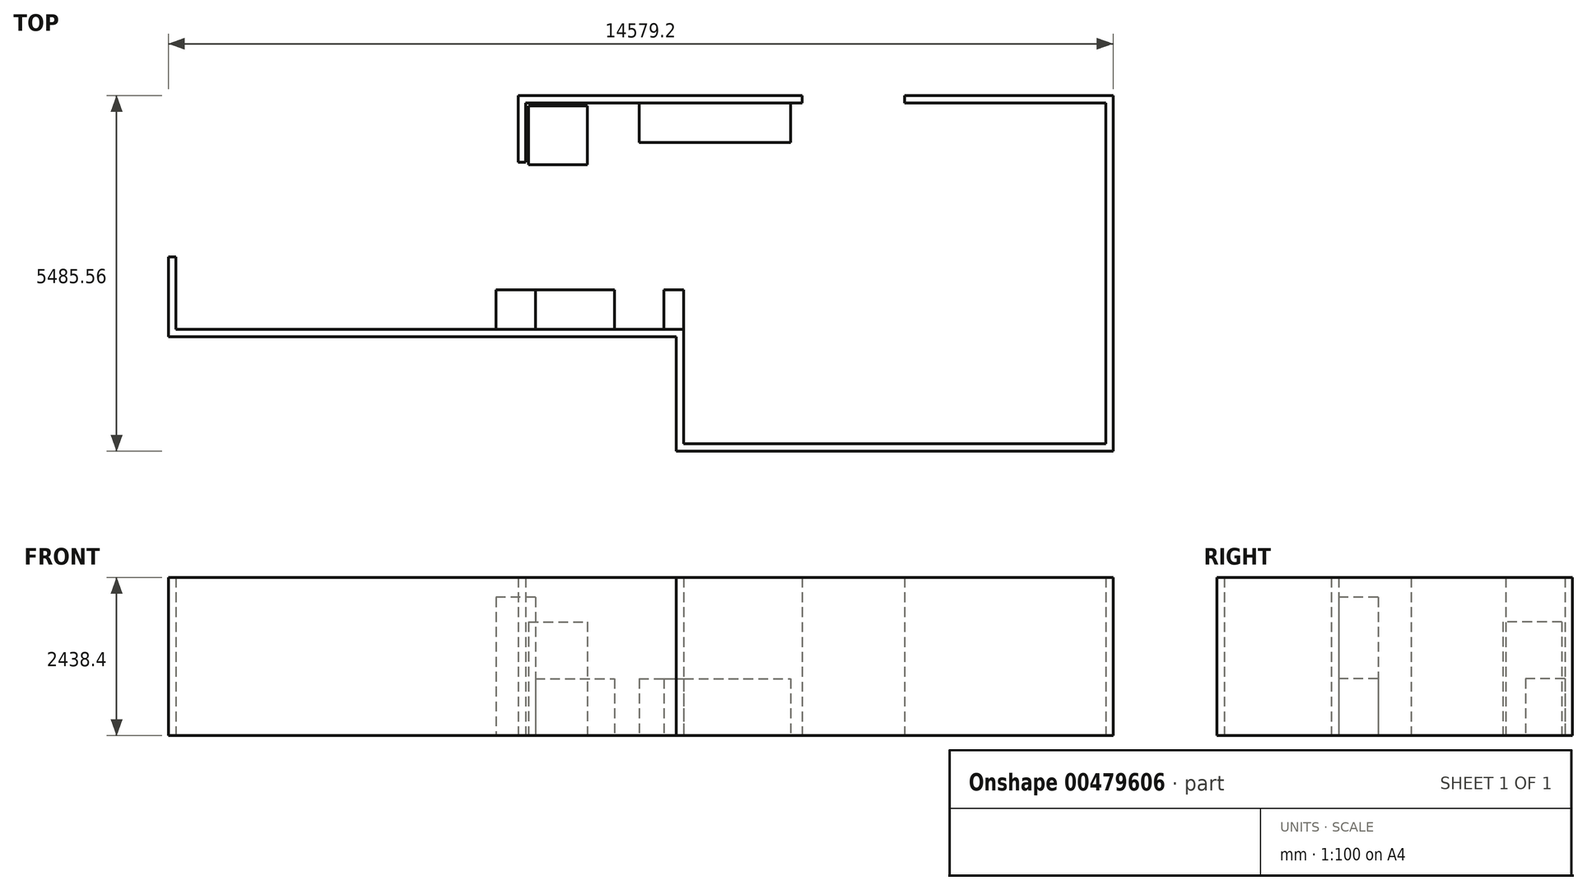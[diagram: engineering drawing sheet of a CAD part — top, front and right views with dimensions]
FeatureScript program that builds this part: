
annotation { "Feature Type Name" : "Feature", "Feature Type Description" : "" }
export const myFeature = defineFeature(function(context is Context, id is Id, definition is map)
    precondition{}
    {
        {
            var Q0;
            Q0=qCreatedBy(makeId("Top.planeOp"),FACE);
            var sketch = newSketch(context, id + "F0", { "sketchPlane" : qUnion([Q0])});
            skLineSegment(sketch, "E0.bottom", {"start": v(-1558.2, 1261.6) * mm, "end": v(-1443.9, 1261.6) * mm});
            skLineSegment(sketch, "E0.top", {"start": v(-1558.2, 232.9) * mm, "end": v(-1443.9, 232.9) * mm});
            skLineSegment(sketch, "E0.left", {"start": v(-1558.2, 1261.6) * mm, "end": v(-1558.2, 232.9) * mm});
            skLineSegment(sketch, "E0.right", {"start": v(-1443.9, 1147.3) * mm, "end": v(-1443.9, 232.9) * mm});
            skLineSegment(sketch, "E1.bottom", {"start": v(-1443.9, 1261.6) * mm, "end": v(2823.3, 1261.6) * mm});
            skLineSegment(sketch, "E1.top", {"start": v(-1443.9, 1147.3) * mm, "end": v(2823.3, 1147.3) * mm});
            skLineSegment(sketch, "E1.right", {"start": v(2823.3, 1261.6) * mm, "end": v(2823.3, 1147.3) * mm});
            skLineSegment(sketch, "E2.bottom", {"start": v(-1558.2, -2345.2) * mm, "end": v(994.5, -2345.2) * mm});
            skLineSegment(sketch, "E2.top", {"start": v(-1558.2, -2459.5) * mm, "end": v(994.5, -2459.5) * mm});
            skLineSegment(sketch, "E2.left", {"start": v(-1558.2, -2345.2) * mm, "end": v(-1558.2, -2459.5) * mm});
            skLineSegment(sketch, "E2.right", {"start": v(994.5, -2345.2) * mm, "end": v(994.5, -2459.5) * mm});
            skLineSegment(sketch, "E3.bottom", {"start": v(-1558.2, -2345.2) * mm, "end": v(-2167.8, -2345.2) * mm});
            skLineSegment(sketch, "E3.top", {"start": v(-1558.2, -2459.5) * mm, "end": v(-2167.8, -2459.5) * mm});
            skLineSegment(sketch, "E3.right", {"start": v(-2167.8, -2345.2) * mm, "end": v(-2167.8, -2459.5) * mm});
            skLineSegment(sketch, "E4.bottom", {"start": v(994.5, -2345.2) * mm, "end": v(880.2, -2345.2) * mm});
            skLineSegment(sketch, "E4.top", {"start": v(994.5, -4223.95) * mm, "end": v(880.2, -4223.95) * mm});
            skLineSegment(sketch, "E4.left", {"start": v(994.5, -2345.2) * mm, "end": v(994.5, -4223.95) * mm});
            skLineSegment(sketch, "E4.right", {"start": v(880.2, -2345.2) * mm, "end": v(880.2, -4223.95) * mm});
            skLineSegment(sketch, "E5.bottom", {"start": v(4408.84, 1261.6) * mm, "end": v(7625.02, 1261.6) * mm});
            skLineSegment(sketch, "E5.top", {"start": v(4408.84, 1147.3) * mm, "end": v(7625.02, 1147.3) * mm});
            skLineSegment(sketch, "E5.left", {"start": v(4408.84, 1261.6) * mm, "end": v(4408.84, 1147.3) * mm});
            skLineSegment(sketch, "E5.right", {"start": v(7625.02, 1261.6) * mm, "end": v(7625.02, 1147.3) * mm});
            skLineSegment(sketch, "E6.bottom", {"start": v(7625.02, 1261.6) * mm, "end": v(7510.72, 1261.6) * mm});
            skLineSegment(sketch, "E6.top", {"start": v(7625.02, -4223.95) * mm, "end": v(7510.72, -4223.95) * mm});
            skLineSegment(sketch, "E6.left", {"start": v(7625.02, 1261.6) * mm, "end": v(7625.02, -4223.95) * mm});
            skLineSegment(sketch, "E6.right", {"start": v(7510.72, 1261.6) * mm, "end": v(7510.72, -4223.95) * mm});
            skLineSegment(sketch, "E7.bottom", {"start": v(7625.02, -4223.95) * mm, "end": v(880.2, -4223.95) * mm});
            skLineSegment(sketch, "E7.top", {"start": v(7625.02, -4109.65) * mm, "end": v(880.2, -4109.65) * mm});
            skLineSegment(sketch, "E7.left", {"start": v(7625.02, -4223.95) * mm, "end": v(7625.02, -4109.65) * mm});
            skLineSegment(sketch, "E7.right", {"start": v(880.2, -4223.95) * mm, "end": v(880.2, -4109.65) * mm});
            skLineSegment(sketch, "E8.bottom", {"start": v(-2167.8, -2345.2) * mm, "end": v(-6839.85, -2345.2) * mm});
            skLineSegment(sketch, "E8.top", {"start": v(-2167.8, -2459.5) * mm, "end": v(-6839.85, -2459.5) * mm});
            skLineSegment(sketch, "E8.right", {"start": v(-6839.85, -2345.2) * mm, "end": v(-6839.85, -2459.5) * mm});
            skLineSegment(sketch, "E9.bottom", {"start": v(-6839.85, -2459.5) * mm, "end": v(-6954.15, -2459.5) * mm});
            skLineSegment(sketch, "E9.top", {"start": v(-6839.85, -1226.01) * mm, "end": v(-6954.15, -1226.01) * mm});
            skLineSegment(sketch, "E9.left", {"start": v(-6839.85, -2459.5) * mm, "end": v(-6839.85, -1226.01) * mm});
            skLineSegment(sketch, "E9.right", {"start": v(-6954.15, -2459.5) * mm, "end": v(-6954.15, -1226.01) * mm});
            skSolve(sketch);
        }
        {
            var Q0;
            Q0 = qSketchRegion(id + "F0", true);
            extrude(context, id + "F1", {"entities" : qUnion([Q0]), "depth" : 2438.4 * mm});
        }
        {
            var Q0;
            Q0=qCreatedBy(makeId("Top.planeOp"),FACE);
            var sketch = newSketch(context, id + "F2", { "sketchPlane" : qUnion([Q0])});
            skLineSegment(sketch, "E10.bottom", {"start": v(-1395.95, 1100.04) * mm, "end": v(-489.43, 1100.04) * mm});
            skLineSegment(sketch, "E10.top", {"start": v(-1395.95, 193.51) * mm, "end": v(-489.43, 193.51) * mm});
            skLineSegment(sketch, "E10.left", {"start": v(-1395.95, 1100.04) * mm, "end": v(-1395.95, 193.51) * mm});
            skLineSegment(sketch, "E10.right", {"start": v(-489.43, 1100.04) * mm, "end": v(-489.43, 193.51) * mm});
            skSolve(sketch);
        }
        {
            var Q0;
            Q0=makeQuery(id+"F2.imprint","IMPRINT",FACE,{"disambiguationData":[TD([[makeQuery(id+"F2.imprint","IMPRINT",EDGE,{"derivedFrom":sQuery(id+"F2.wireOp",EDGE,"E10.bottom")}),-1.0]])]});
            extrude(context, id + "F3", {"entities" : qUnion([Q0]), "depth" : 1752.6 * mm});
        }
        {
            var Q0;
            Q0=qCreatedBy(makeId("Top.planeOp"),FACE);
            var sketch = newSketch(context, id + "F4", { "sketchPlane" : qUnion([Q0])});
            skLineSegment(sketch, "E11.bottom", {"start": v(-986.7, -1735.6) * mm, "end": v(-72.3, -1735.6) * mm});
            skLineSegment(sketch, "E11.top", {"start": v(-986.7, -2345.2) * mm, "end": v(-72.3, -2345.2) * mm});
            skLineSegment(sketch, "E11.left", {"start": v(-986.7, -1735.6) * mm, "end": v(-986.7, -2345.2) * mm});
            skLineSegment(sketch, "E11.right", {"start": v(-72.3, -1735.6) * mm, "end": v(-72.3, -2345.2) * mm});
            skLineSegment(sketch, "E12.bottom", {"start": v(689.7, -1735.6) * mm, "end": v(994.5, -1735.6) * mm});
            skLineSegment(sketch, "E12.top", {"start": v(689.7, -2345.2) * mm, "end": v(994.5, -2345.2) * mm});
            skLineSegment(sketch, "E12.left", {"start": v(689.7, -1735.6) * mm, "end": v(689.7, -2345.2) * mm});
            skLineSegment(sketch, "E12.right", {"start": v(994.5, -1735.6) * mm, "end": v(994.5, -2345.2) * mm});
            skLineSegment(sketch, "E13.bottom", {"start": v(-986.7, -1735.6) * mm, "end": v(-1291.5, -1735.6) * mm});
            skLineSegment(sketch, "E13.top", {"start": v(-986.7, -2345.2) * mm, "end": v(-1291.5, -2345.2) * mm});
            skLineSegment(sketch, "E13.right", {"start": v(-1291.5, -1735.6) * mm, "end": v(-1291.5, -2345.2) * mm});
            skLineSegment(sketch, "E14.bottom", {"start": v(310.67, 1147.3) * mm, "end": v(717.07, 1147.3) * mm});
            skLineSegment(sketch, "E14.top", {"start": v(310.67, 537.7) * mm, "end": v(717.07, 537.7) * mm});
            skLineSegment(sketch, "E14.left", {"start": v(310.67, 1147.3) * mm, "end": v(310.67, 537.7) * mm});
            skLineSegment(sketch, "E14.right", {"start": v(717.07, 1147.3) * mm, "end": v(717.07, 537.7) * mm});
            skLineSegment(sketch, "E15.bottom", {"start": v(717.07, 1147.3) * mm, "end": v(1631.47, 1147.3) * mm});
            skLineSegment(sketch, "E15.top", {"start": v(717.07, 537.7) * mm, "end": v(1631.47, 537.7) * mm});
            skLineSegment(sketch, "E15.right", {"start": v(1631.47, 1147.3) * mm, "end": v(1631.47, 537.7) * mm});
            skLineSegment(sketch, "E16.bottom", {"start": v(1631.47, 1147.3) * mm, "end": v(2037.87, 1147.3) * mm});
            skLineSegment(sketch, "E16.top", {"start": v(1631.47, 537.7) * mm, "end": v(2037.87, 537.7) * mm});
            skLineSegment(sketch, "E16.right", {"start": v(2037.87, 1147.3) * mm, "end": v(2037.87, 537.7) * mm});
            skLineSegment(sketch, "E17.bottom", {"start": v(2037.87, 1147.3) * mm, "end": v(2647.47, 1147.3) * mm});
            skLineSegment(sketch, "E17.top", {"start": v(2037.87, 537.7) * mm, "end": v(2647.47, 537.7) * mm});
            skLineSegment(sketch, "E17.right", {"start": v(2647.47, 1147.3) * mm, "end": v(2647.47, 537.7) * mm});
            skSolve(sketch);
        }
        {
            var Q0;
            Q0 = qSketchRegion(id + "F4", true);
            extrude(context, id + "F5", {"entities" : qUnion([Q0]), "depth" : 876.3 * mm});
        }
        {
            var Q0;
            Q0=qCreatedBy(makeId("Top.planeOp"),FACE);
            var sketch = newSketch(context, id + "F6", { "sketchPlane" : qUnion([Q0])});
            skLineSegment(sketch, "E18.bottom", {"start": v(-1291.5, -1735.6) * mm, "end": v(-1901.1, -1735.6) * mm});
            skLineSegment(sketch, "E18.top", {"start": v(-1291.5, -2345.2) * mm, "end": v(-1901.1, -2345.2) * mm});
            skLineSegment(sketch, "E18.left", {"start": v(-1291.5, -1735.6) * mm, "end": v(-1291.5, -2345.2) * mm});
            skLineSegment(sketch, "E18.right", {"start": v(-1901.1, -1735.6) * mm, "end": v(-1901.1, -2345.2) * mm});
            skSolve(sketch);
        }
        {
            var Q0;
            Q0 = qSketchRegion(id + "F6", true);
            extrude(context, id + "F7", {"entities" : qUnion([Q0]), "depth" : 2133.6 * mm});
        }
    });
